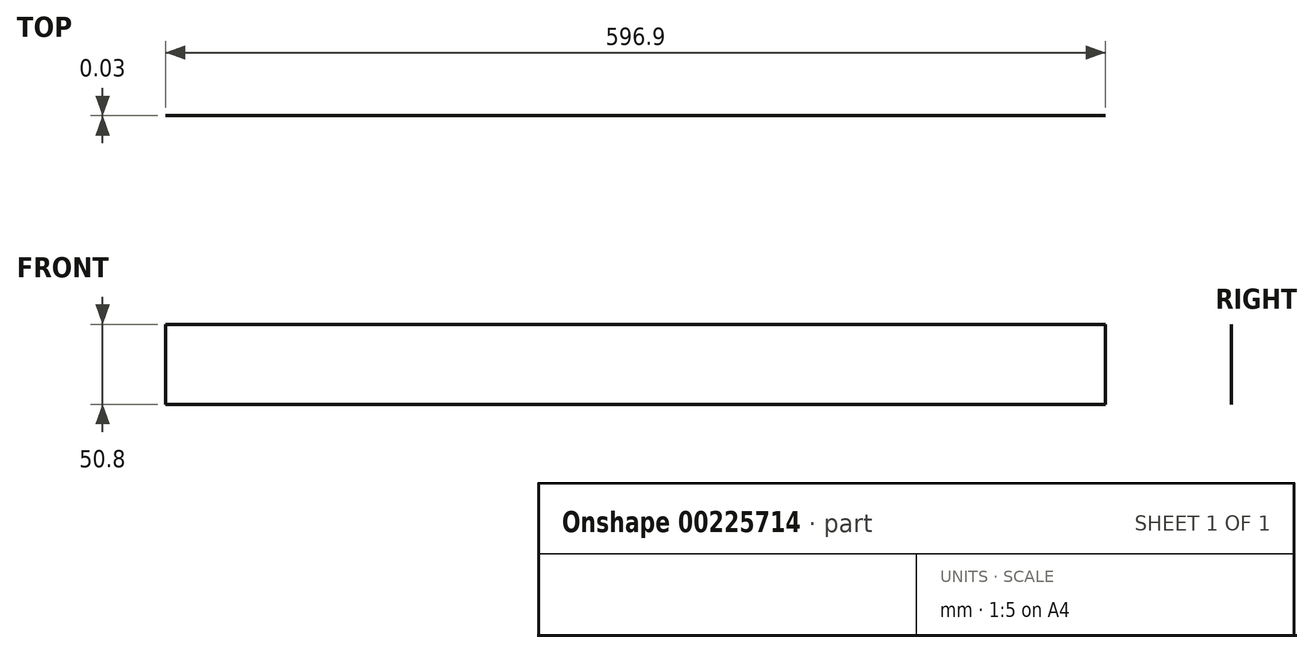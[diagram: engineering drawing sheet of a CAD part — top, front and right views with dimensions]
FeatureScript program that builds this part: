
annotation { "Feature Type Name" : "Feature", "Feature Type Description" : "" }
export const myFeature = defineFeature(function(context is Context, id is Id, definition is map)
    precondition{}
    {
        {
            var Q0;
            Q0=qCreatedBy(makeId("Front.planeOp"),FACE);
            var sketch = newSketch(context, id + "F0", { "sketchPlane" : qUnion([Q0])});
            skLineSegment(sketch, "E0.bottom", {"start": v(-117.2, 28.03) * mm, "end": v(479.7, 28.03) * mm});
            skLineSegment(sketch, "E0.top", {"start": v(-117.2, -22.77) * mm, "end": v(479.7, -22.77) * mm});
            skLineSegment(sketch, "E0.left", {"start": v(-117.2, 28.03) * mm, "end": v(-117.2, -22.77) * mm});
            skLineSegment(sketch, "E0.right", {"start": v(479.7, 28.03) * mm, "end": v(479.7, -22.77) * mm});
            skSolve(sketch);
        }
        {
            var Q0;
            Q0=makeQuery(id+"F0.imprint","IMPRINT",FACE,{"disambiguationData":[TD([[makeQuery(id+"F0.imprint","IMPRINT",EDGE,{"derivedFrom":sQuery(id+"F0.wireOp",EDGE,"E0.bottom")}),-1.0]])]});
            extrude(context, id + "F1", {"entities" : qUnion([Q0]), "depth" : 23 / 812.8 * mm});
        }
    });
